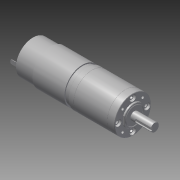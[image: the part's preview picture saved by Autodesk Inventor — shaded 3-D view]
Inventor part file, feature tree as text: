
AUTODESK INVENTOR PART (.ipt)
format: ipt  version: 2013 (Build 170138000, 138)  size: 288,768 bytes
history: native  units: in
note: dims shown in document units (in); Inventor stores cm internally (conversion verified against a paired STEP export)
features: mirror x1, other x1, imported_body x1
ambient origin geometry x8: Origin, YZ Plane, XZ Plane, XY Plane, X Axis, Y Axis, Z Axis, Center Point
feature tree (3):
  mirror  "Mirror2"
  other  "PG-711"
  imported_body  "Base1"
